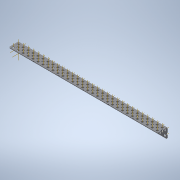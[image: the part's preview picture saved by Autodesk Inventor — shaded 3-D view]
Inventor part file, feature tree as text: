
AUTODESK INVENTOR PART (.ipt)
format: ipt  version: 2020 (Build 240168000, 168)  size: 2,348,544 bytes
history: native  units: in
note: dims shown in document units (in); Inventor stores cm internally (conversion verified against a paired STEP export)
features: other x185, pattern_linear x4, sheet_metal_op x1, extrude x1, plane x1, split x1, imported_body x1, sketch x1
ambient origin geometry x8: Origin, YZ Plane, XZ Plane, XY Plane, X Axis, Y Axis, Z Axis, Center Point
bodies: Body1 (feature_tree)
feature tree (195):
  sheet_metal_op  "Fold1"
  other  "L-Channel"
  extrude  "length cut"  Depth=0.5in
  other  "top out axis"
  other  "top inner axis"
  other  "back out axis"
  other  "back inner axis"
  pattern_linear  "top outer axes"  Count1=2 Spacing1=0.5in
  pattern_linear  "top inner axes"  Spacing1=0.5in  [1 undecoded]
  pattern_linear  "back outer axes"  Count1=2 Spacing1=0.5in
  pattern_linear  "back inner axes"  Spacing1=0.5in  [1 undecoded]
  other  "right plane"
  plane  "Work Plane3"
  split  "Split1"
  imported_body  "Base1"
  sketch  "Sketch1"  dims[d1=0.0in d4=0.5in d5=0.7874in d7=0.5in d10=0.5in d13=0.5in d14=0.7874in d16=0.5in d19=0.5in d20=-17.5in d21=0.0in d22=0.0in d23=0.0in d24=0.0in d25=0.0in d26=0.0in]
  other  "Work Point1"
  other  "Work Point2"
  other  "Work Point3"
  other  "Work Point4"
  other  "Work Axis5"
  other  "Work Axis6"
  other  "Work Axis7"
  other  "Work Axis8"
  other  "Work Axis11"
  other  "Work Axis12"
  other  "Work Axis13"
  other  "Work Axis14"
  other  "Work Axis15"
  other  "Work Axis18"
  other  "Work Axis19"
  other  "Work Axis20"
  other  "Work Axis23"
  other  "Work Axis24"
  other  "Work Axis25"
  other  "Work Axis26"
  other  "Work Axis29"
  other  "Work Axis30"
  other  "Work Axis31"
  other  "Work Axis32"
  other  "Work Axis33"
  other  "Work Axis36"
  other  "Work Axis37"
  other  "Work Axis38"
  other  "Work Axis41"
  other  "Work Axis42"
  other  "Work Axis43"
  other  "Work Axis44"
  other  "Work Axis45"
  other  "Work Axis46"
  other  "Work Axis47"
  other  "Work Axis48"
  other  "Work Axis49"
  other  "Work Axis50"
  other  "Work Axis51"
  other  "Work Axis52"
  other  "Work Axis53"
  other  "Work Axis54"
  other  "Work Axis55"
  other  "Work Axis56"
  other  "Work Axis57"
  other  "Work Axis58"
  other  "Work Axis59"
  other  "Work Axis60"
  other  "Work Axis61"
  other  "Work Axis62"
  other  "Work Axis63"
  other  "Work Axis64"
  other  "Work Axis65"
  other  "Work Axis66"
  other  "Work Axis67"
  other  "Work Axis68"
  other  "Work Axis69"
  other  "Work Axis70"
  other  "Work Axis71"
  other  "Work Axis72"
  other  "Work Axis73"
  other  "Work Axis74"
  other  "Work Axis75"
  other  "Work Axis76"
  other  "Work Axis77"
  other  "Work Axis78"
  other  "Work Axis79"
  other  "Work Axis80"
  other  "Work Axis81"
  other  "Work Axis82"
  other  "Work Axis83"
  other  "Work Axis84"
  other  "Work Axis85"
  other  "Work Axis86"
  other  "Work Axis87"
  other  "Work Axis88"
  other  "Work Axis89"
  other  "Work Axis90"
  other  "Work Axis91"
  other  "Work Axis92"
  other  "Work Axis93"
  other  "Work Axis94"
  other  "Work Axis95"
  other  "Work Axis96"
  other  "Work Axis97"
  other  "Work Axis98"
  other  "Work Axis99"
  other  "Work Axis100"
  other  "Work Axis101"
  other  "Work Axis102"
  other  "Work Axis103"
  other  "Work Axis104"
  other  "Work Axis105"
  other  "Work Axis106"
  other  "Work Axis107"
  other  "Work Axis108"
  other  "Work Axis109"
  other  "Work Axis110"
  other  "Work Axis111"
  other  "Work Axis112"
  other  "Work Axis113"
  other  "Work Axis114"
  other  "Work Axis115"
  other  "Work Axis116"
  other  "Work Axis117"
  other  "Work Axis118"
  other  "Work Axis119"
  other  "Work Axis120"
  other  "Work Axis121"
  other  "Work Axis122"
  other  "Work Axis123"
  other  "Work Axis124"
  other  "Work Axis125"
  other  "Work Axis126"
  other  "Work Axis127"
  other  "Work Axis128"
  other  "Work Axis129"
  other  "Work Axis130"
  other  "Work Axis131"
  other  "Work Axis132"
  other  "Work Axis133"
  other  "Work Axis134"
  other  "Work Axis135"
  other  "Work Axis136"
  other  "Work Axis137"
  other  "Work Axis138"
  other  "Work Axis139"
  other  "Work Axis140"
  other  "Work Axis141"
  other  "Work Axis142"
  other  "Work Axis143"
  other  "Work Axis144"
  other  "Work Axis145"
  other  "Work Axis146"
  other  "Work Axis147"
  other  "Work Axis148"
  other  "Work Axis149"
  other  "Work Axis150"
  other  "Work Axis151"
  other  "Work Axis152"
  other  "Work Axis153"
  other  "Work Axis154"
  other  "Work Axis155"
  other  "Work Axis156"
  other  "Work Axis157"
  other  "Work Axis158"
  other  "Work Axis159"
  other  "Work Axis160"
  other  "left plane"
  other  "Work Axis161"
  other  "Work Axis162"
  other  "Work Axis163"
  other  "Work Axis164"
  other  "Work Axis165"
  other  "Work Axis166"
  other  "Work Axis167"
  other  "Work Axis168"
  other  "Work Axis169"
  other  "Work Axis170"
  other  "Work Axis171"
  other  "Work Axis172"
  other  "Work Axis173"
  other  "Work Axis174"
  other  "Work Axis175"
  other  "Work Axis176"
  other  "Work Axis177"
  other  "Work Axis178"
  other  "Work Axis179"
  other  "Work Axis180"
  other  "Work Axis181"
  other  "Work Axis182"
  other  "Work Axis183"
  other  "Work Axis184"
  other  "Work Axis185"
  other  "Work Axis191"
  other  "Work Axis197"
  other  "Work Axis203"
  other  "Work Axis209"
  other  "Work Axis215"
note: 2 required parameter values undecoded (feature->parameter linkage not recoverable at this tier; creation-order binding heuristic only, values carry confidence <= 0.55)
